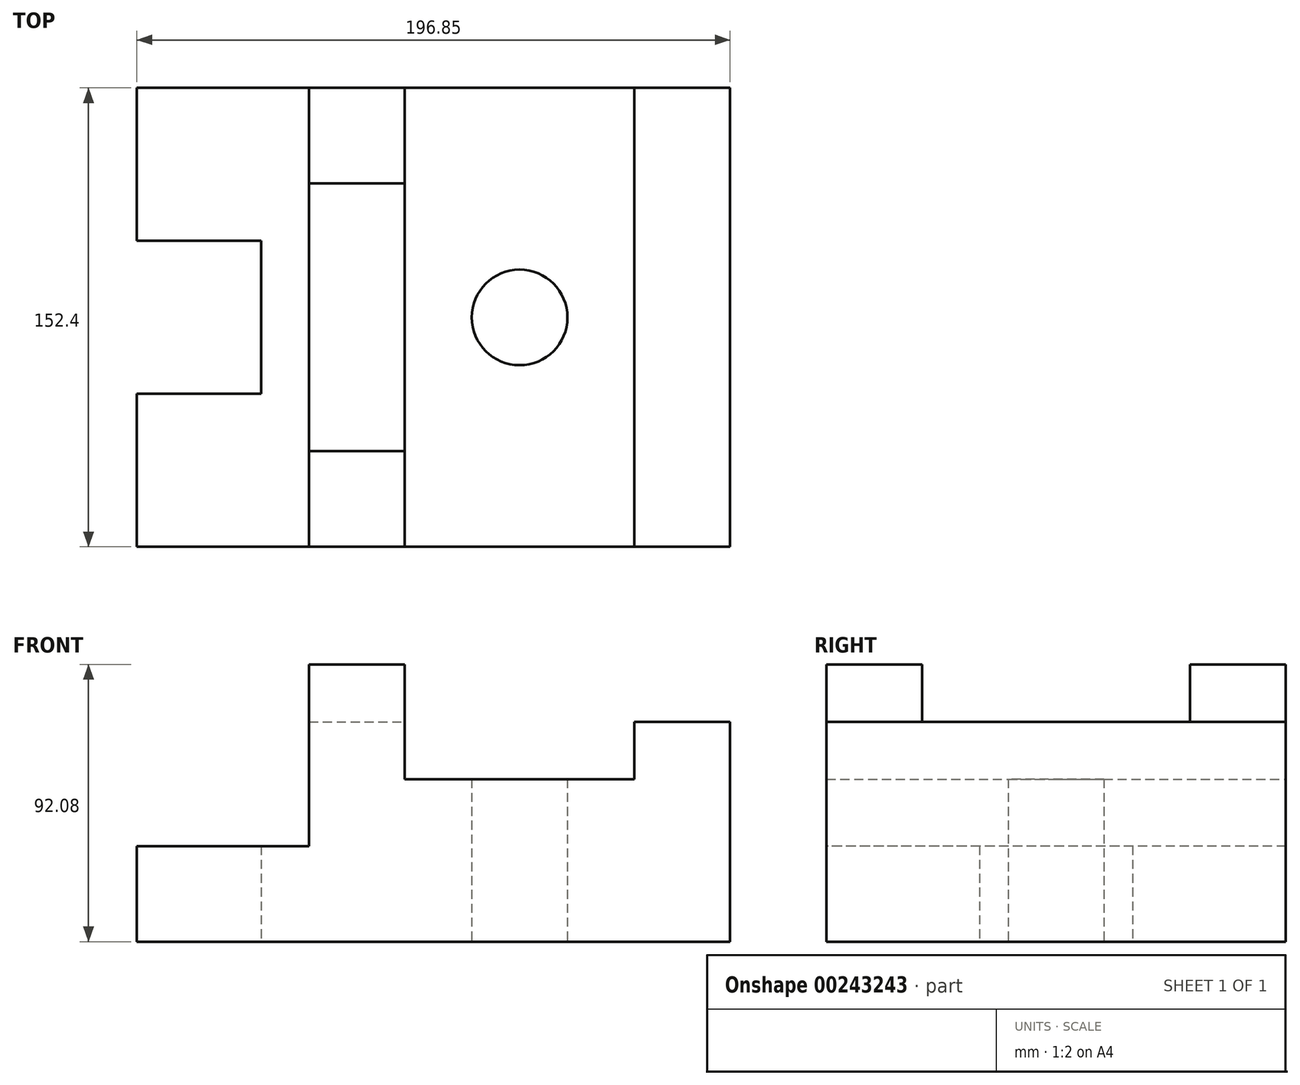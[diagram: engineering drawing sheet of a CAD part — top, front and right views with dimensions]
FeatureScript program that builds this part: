
annotation { "Feature Type Name" : "Feature", "Feature Type Description" : "" }
export const myFeature = defineFeature(function(context is Context, id is Id, definition is map)
    precondition{}
    {
        {
            var Q0;
            Q0=qCreatedBy(makeId("Top.planeOp"),FACE);
            var sketch = newSketch(context, id + "F0", { "sketchPlane" : qUnion([Q0])});
            skLineSegment(sketch, "E0.bottom", {"start": v(0, 0) * mm, "end": v(254, 0) * mm});
            skLineSegment(sketch, "E0.top", {"start": v(0, -152.4) * mm, "end": v(254, -152.4) * mm});
            skLineSegment(sketch, "E0.left", {"start": v(0, 0) * mm, "end": v(0, -152.4) * mm});
            skLineSegment(sketch, "E0.right", {"start": v(254, 0) * mm, "end": v(254, -152.4) * mm});
            skLineSegment(sketch, "E1.bottom", {"start": v(254, 0) * mm, "end": v(196.85, 0) * mm});
            skLineSegment(sketch, "E1.top", {"start": v(254, -152.4) * mm, "end": v(196.85, -152.4) * mm});
            skLineSegment(sketch, "E1.right", {"start": v(196.85, 0) * mm, "end": v(196.85, -152.4) * mm});
            skLineSegment(sketch, "E2", {"start": v(127, 0) * mm, "end": v(127, -152.4) * mm});
            skLineSegment(sketch, "E3.MirrorCS", {"start": v(57.15, 0) * mm, "end": v(57.15, -152.4) * mm});
            skLineSegment(sketch, "E4.bottom", {"start": v(254, -50.8) * mm, "end": v(212.72, -50.8) * mm});
            skLineSegment(sketch, "E4.top", {"start": v(254, -101.6) * mm, "end": v(212.72, -101.6) * mm});
            skLineSegment(sketch, "E4.left", {"start": v(254, -50.8) * mm, "end": v(254, -101.6) * mm});
            skLineSegment(sketch, "E4.right", {"start": v(212.72, -50.8) * mm, "end": v(212.72, -101.6) * mm});
            skLineSegment(sketch, "E5", {"start": v(254, -101.6) * mm, "end": v(254, -152.4) * mm});
            skLineSegment(sketch, "E6.MirrorCS", {"start": v(254, -152.4) * mm, "end": v(0, -152.4) * mm});
            skLineSegment(sketch, "E7.MirrorCS", {"start": v(41.28, -50.8) * mm, "end": v(41.27, -101.6) * mm});
            skLineSegment(sketch, "E8.MirrorCS", {"start": v(0, -101.6) * mm, "end": v(41.28, -101.6) * mm});
            skLineSegment(sketch, "E9.MirrorCS", {"start": v(0, -50.8) * mm, "end": v(41.28, -50.8) * mm});
            skLineSegment(sketch, "E10.bottom", {"start": v(196.85, -152.4) * mm, "end": v(165.1, -152.4) * mm});
            skLineSegment(sketch, "E10.top", {"start": v(196.85, -120.65) * mm, "end": v(165.1, -120.65) * mm});
            skLineSegment(sketch, "E10.left", {"start": v(196.85, -152.4) * mm, "end": v(196.85, -120.65) * mm});
            skLineSegment(sketch, "E10.right", {"start": v(165.1, -152.4) * mm, "end": v(165.1, -120.65) * mm});
            skLineSegment(sketch, "E11.MirrorCS", {"start": v(88.9, -152.4) * mm, "end": v(88.9, -120.65) * mm});
            skLineSegment(sketch, "E12.MirrorCS", {"start": v(57.15, -120.65) * mm, "end": v(88.9, -120.65) * mm});
            skLineSegment(sketch, "E13.bottom", {"start": v(196.85, 0) * mm, "end": v(165.1, 0) * mm});
            skLineSegment(sketch, "E13.top", {"start": v(196.85, -31.75) * mm, "end": v(165.1, -31.75) * mm});
            skLineSegment(sketch, "E13.left", {"start": v(196.85, 0) * mm, "end": v(196.85, -31.75) * mm});
            skLineSegment(sketch, "E13.right", {"start": v(165.1, 0) * mm, "end": v(165.1, -31.75) * mm});
            skLineSegment(sketch, "E14.MirrorCS", {"start": v(88.9, 0) * mm, "end": v(88.9, -31.75) * mm});
            skLineSegment(sketch, "E15.MirrorCS", {"start": v(57.15, -31.75) * mm, "end": v(88.9, -31.75) * mm});
            skLineSegment(sketch, "E16", {"start": v(88.9, -31.75) * mm, "end": v(88.9, -120.65) * mm});
            skLineSegment(sketch, "E17", {"start": v(165.1, -31.75) * mm, "end": v(165.1, -120.65) * mm});
            skCircle(sketch, "E18", {"center": v(127, -76.2) * mm, "radius": 15.88 * mm});
            skSolve(sketch);
        }
        {
            var Q0;
            {var subQ8=sQuery(id+"F0.wireOp",EDGE,"E11.MirrorCS");Q0=makeQuery(id+"F0.imprint","IMPRINT",FACE,{"disambiguationData":[TD([[makeQuery(id+"F0.imprint","IMPRINT",EDGE,{"derivedFrom":subQ8}),-1.0]])]});}
            var Q1;
            {var subQ3=sQuery(id+"F0.wireOp",EDGE,"E10.right");Q1=makeQuery(id+"F0.imprint","IMPRINT",FACE,{"disambiguationData":[TD([[makeQuery(id+"F0.imprint","IMPRINT",EDGE,{"derivedFrom":subQ3}),1.0]])]});}
            extrude(context, id + "F1", {"entities" : qUnion([Q0, Q1]), "depth" : 53.97 * mm});
        }
        {
            var Q0;
            Q0=makeQuery(id+"F0.imprint","IMPRINT",FACE,{"disambiguationData":[TD([[makeQuery(id+"F0.imprint","IMPRINT",EDGE,{"derivedFrom":sQuery(id+"F0.wireOp",EDGE,"E7.MirrorCS")}),1.0]])]});
            var Q1;
            Q1=makeQuery(id+"F0.imprint","IMPRINT",FACE,{"disambiguationData":[TD([[makeQuery(id+"F0.imprint","IMPRINT",EDGE,{"derivedFrom":sQuery(id+"F0.wireOp",EDGE,"E1.bottom")}),1.0]])]});
            extrude(context, id + "F2", {"entities" : qUnion([Q0, Q1]), "operationType" : NewBodyOperationType.ADD, "depth" : 31.75 * mm});
        }
        {
            var Q0;
            {var subQ4=sQuery(id+"F0.wireOp",EDGE,"E11.MirrorCS");Q0=makeQuery(id+"F0.imprint","IMPRINT",FACE,{"disambiguationData":[TD([[makeQuery(id+"F0.imprint","IMPRINT",EDGE,{"derivedFrom":subQ4}),1.0]])]});}
            var Q1;
            {var subQ3=sQuery(id+"F0.wireOp",EDGE,"E14.MirrorCS");Q1=makeQuery(id+"F0.imprint","IMPRINT",FACE,{"disambiguationData":[TD([[makeQuery(id+"F0.imprint","IMPRINT",EDGE,{"derivedFrom":subQ3}),-1.0]])]});}
            var Q2;
            Q2=makeQuery(id+"F0.imprint","IMPRINT",FACE,{"disambiguationData":[TD([[makeQuery(id+"F0.imprint","IMPRINT",EDGE,{"derivedFrom":sQuery(id+"F0.wireOp",EDGE,"E13.bottom")}),1.0]])]});
            var Q3;
            Q3=makeQuery(id+"F0.imprint","IMPRINT",FACE,{"disambiguationData":[TD([[makeQuery(id+"F0.imprint","IMPRINT",EDGE,{"derivedFrom":sQuery(id+"F0.wireOp",EDGE,"E10.bottom")}),-1.0]])]});
            extrude(context, id + "F3", {"entities" : qUnion([Q0, Q1, Q2, Q3]), "operationType" : NewBodyOperationType.ADD, "depth" : 92.07 * mm});
        }
        {
            var Q0;
            {var subQ0=sQuery(id+"F0.wireOp",EDGE,"E12.MirrorCS");Q0=makeQuery(id+"F0.imprint","IMPRINT",FACE,{"disambiguationData":[TD([[makeQuery(id+"F0.imprint","IMPRINT",EDGE,{"derivedFrom":subQ0}),1.0]])]});}
            var Q1;
            Q1=makeQuery(id+"F0.imprint","IMPRINT",FACE,{"disambiguationData":[TD([[makeQuery(id+"F0.imprint","IMPRINT",EDGE,{"derivedFrom":sQuery(id+"F0.wireOp",EDGE,"E1.right")}),-1.0]])]});
            extrude(context, id + "F4", {"entities" : qUnion([Q0, Q1]), "operationType" : NewBodyOperationType.ADD, "depth" : 73.02 * mm});
        }
    });
